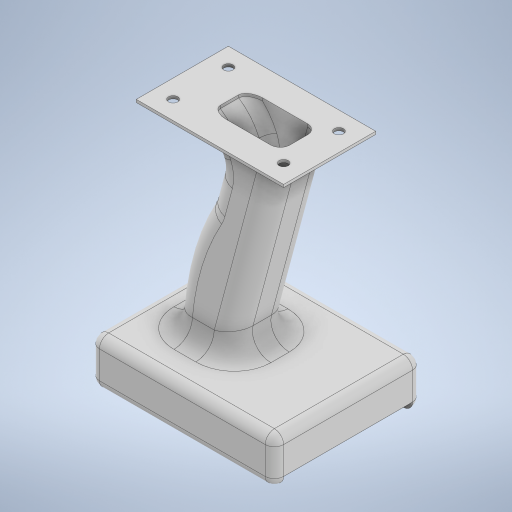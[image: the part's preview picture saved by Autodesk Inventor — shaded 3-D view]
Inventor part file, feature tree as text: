
AUTODESK INVENTOR PART (.ipt)
format: ipt  version: 2023.2 (Build 272271030, 271C)  size: 540,672 bytes
history: native  units: mm
features: sketch x9, extrude x7, fillet x4, projected_geometry x2, shell x1
ambient origin geometry x8: Origin, YZ Plane, XZ Plane, XY Plane, X Axis, Y Axis, Z Axis, Center Point
bodies: Solid1 (feature_tree)
feature tree (23):
  extrude  "Extrusion1"  Depth=80.0mm
  fillet  "Fillet1"  Radius=25.0mm
  extrude  "Extrusion2"  Depth=62.0mm
  extrude  "Extrusion3"  Depth=10.0mm TaperAngle=0.0deg
  extrude  "Extrusion4"  Depth=30.0mm TaperAngle=0.0deg
  sketch  "Sketch7"  dims[d34=75.0deg d35=70.0mm d36=140.0mm d37=25.0mm d38=10.0mm d39=10.0mm]
  extrude  "Extrusion7"  Depth=10.0mm
  sketch  "Sketch9"  dims[d57=50.0mm d58=1.5mm d59=0.0mm]
  fillet  "Fillet2"  Radius=140.0mm
  fillet  "Fillet3"  Radius=25.0mm
  fillet  "Fillet4"  Radius=10.0mm
  shell  "Shell1"  Thickness=10.0mm
  extrude  "Extrusion11"  Depth=10.0mm
  extrude  "Extrusion12"  Depth=1.5mm TaperAngle=0.0deg
  sketch  "Sketch1"  dims[d0=100.0mm d1=80.0mm d2=25.0mm d3=0.0mm]
  sketch  "Sketch2"  dims[d4=5.0mm d5=62.0mm]
  projected_geometry  "Projected Loop1"
  sketch  "Sketch3"  dims[d6=75.0mm d7=0.0mm d8=10.0mm d9=0.0mm]
  projected_geometry  "Projected Loop2"
  sketch  "Sketch4"  dims[d10=70.0mm d11=0.0mm d26=30.0mm d27=0.0mm]
  sketch  "Sketch8"  dims[d40=10.0mm d41=5.0mm]
  sketch  "Sketch16"  dims[d61=5.0mm]
  sketch  "Sketch17"  dims[d62=1.5mm d63=0.0mm d64=0.5mm d65=0.872665mm]
